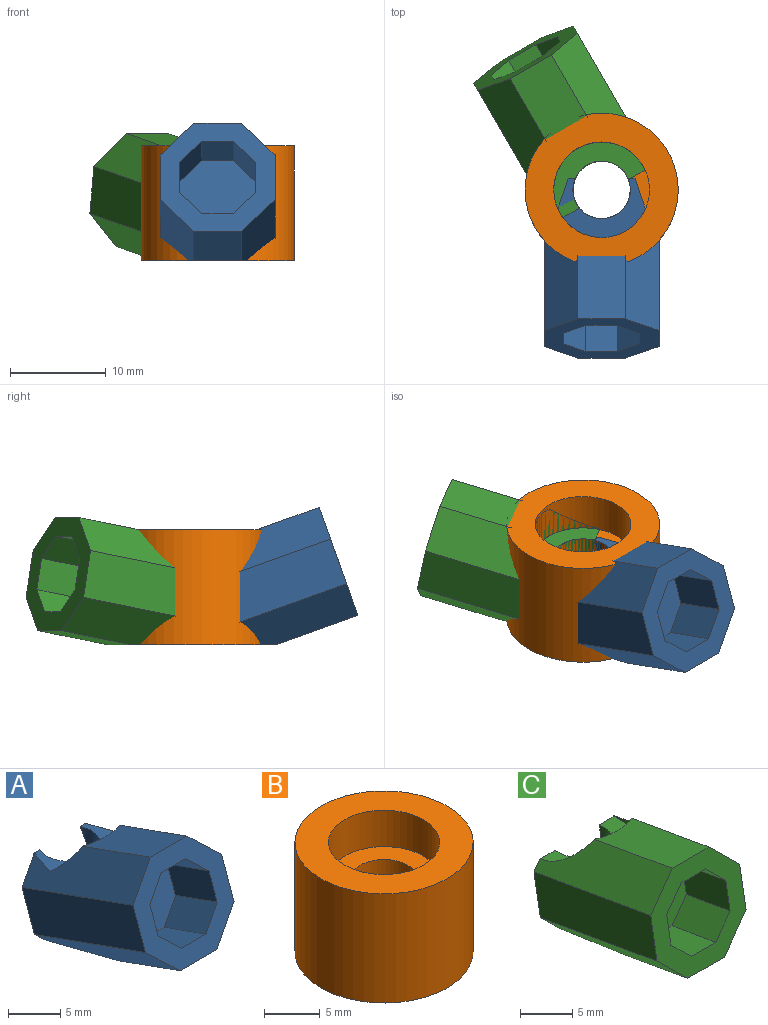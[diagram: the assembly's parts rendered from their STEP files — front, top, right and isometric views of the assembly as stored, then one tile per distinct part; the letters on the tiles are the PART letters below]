
ASSEMBLY  parts=3 mates=2
PART A: 24 faces, bbox 12x18.8x14.4 mm
  f0: plane 8x3.5mm, normal (0,0.94,-0.34), area 22.9mm2, adj f1,f8,f17,f20,f22,f23
  f1: plane 15.91x8.71mm, normal (0.71,0.24,0.67), area 67.3mm2, adj f0,f4,f17,f18,f21,f22
  f2: plane 15.91x8.71mm, normal (-0.71,0.24,0.67), area 67.3mm2, adj f3,f4,f5,f18,f21,f22
  f3: plane 8x3.5mm, normal (0,0.94,-0.34), area 22.9mm2, adj f2,f5,f6,f20,f22,f23
  f4: plane 9.16x4.97mm, normal (0,0.34,0.94), area 46mm2, adj f1,f2,f18,f21
  f5: plane 16.74x10.09mm, normal (-1,0,0), area 79.5mm2, adj f2,f3,f6,f18
  f6: plane 16.25x6.36mm, normal (-0.71,-0.24,-0.67), area 67.2mm2, adj f3,f5,f7,f18,f23
  f7: plane 8.51x4.97mm, normal (0,-0.34,-0.94), area 45mm2, adj f6,f8,f18,f23
  f8: plane 16.25x6.36mm, normal (0.71,-0.24,-0.67), area 67.2mm2, adj f0,f7,f17,f18,f23
  f9: plane 5.65x3.31mm, normal (0,-0.34,-0.94), area 19.9mm2, adj f10,f16,f18,f19
  f10: plane 6.44x4.23mm, normal (-0.71,-0.24,-0.67), area 19.9mm2, adj f9,f11,f18,f19
  f11: plane 6.77x5.15mm, normal (-1,0,0), area 19.9mm2, adj f10,f12,f18,f19
  f12: plane 6.44x4.23mm, normal (-0.71,0.24,0.67), area 19.9mm2, adj f11,f13,f18,f19
  f13: plane 5.65x3.31mm, normal (0,0.34,0.94), area 19.9mm2, adj f12,f14,f18,f19
  f14: plane 6.44x4.23mm, normal (0.71,0.24,0.67), area 19.9mm2, adj f13,f15,f18,f19
  f15: plane 6.77x5.15mm, normal (1,0,0), area 19.9mm2, adj f14,f16,f18,f19
  f16: plane 6.44x4.23mm, normal (0.71,-0.24,-0.67), area 19.9mm2, adj f9,f15,f18,f19
  f17: plane 16.74x10.09mm, normal (1,0,0), area 79.5mm2, adj f0,f1,f8,f18
  f18: plane 12x11.29mm, normal (0,-0.94,0.34), area 66.3mm2, adj f1,f2,f4,f5,f6,f7,f8,f9
  f19: plane 8x7.53mm, normal (0,-0.94,0.34), area 53mm2, adj f9,f10,f11,f12,f13,f14,f15,f16
  f20: cylinder r=3mm len=8mm, axis (0,0,1), area 71.8mm2, adj f0,f3,f22,f23
  f21: cylinder r=5mm len=9.16mm, axis (0,0,-1), area 25.9mm2, adj f1,f2,f4,f22
  f22: plane 9.16x6.22mm, normal (0,0,1), area 24.5mm2, adj f0,f1,f2,f3,f20,f21
  f23: plane 9.97x7.39mm, normal (0,0,-1), area 50.4mm2, adj f0,f3,f6,f7,f8,f20
PART B: 6 faces, bbox 16x16x12 mm
  f0: cylinder r=3mm len=8mm, axis (0,0,1), area 150.8mm2, adj f3,f5
  f1: cylinder r=8mm len=16mm, axis (0,0,-1), area 603.2mm2, adj f2,f3
  f2: plane 16x16mm, normal (0,0,1), area 122.5mm2, adj f1,f4
  f3: plane 16x16mm, normal (0,0,-1), area 172.8mm2, adj f0,f1
  f4: cylinder r=5mm len=10mm, axis (0,0,-1), area 125.7mm2, adj f2,f5
  f5: plane 10x10mm, normal (0,0,1), area 50.3mm2, adj f0,f4
PART C: 24 faces, bbox 12x17.4x13.3 mm
  f0: plane 8.07x3.15mm, normal (0,0.98,-0.17), area 21.8mm2, adj f2,f8,f17,f20,f21,f22,f23
  f1: plane 8.07x3.15mm, normal (0,0.98,-0.17), area 21.8mm2, adj f4,f5,f6,f20,f21,f22,f23
  f2: plane 15.93x6.24mm, normal (0.71,0.12,0.7), area 65.9mm2, adj f0,f3,f17,f18,f21
  f3: plane 10.5x4.97mm, normal (0,0.17,0.98), area 50.7mm2, adj f2,f4,f18,f21
  f4: plane 15.93x6.24mm, normal (-0.71,0.12,0.7), area 65.9mm2, adj f1,f3,f5,f18,f21
  f5: plane 16.62x7.67mm, normal (-1,0,0), area 79.5mm2, adj f1,f4,f6,f18
  f6: plane 16.37x4.94mm, normal (-0.71,-0.12,-0.7), area 72.6mm2, adj f1,f5,f7,f18,f23
  f7: plane 8.4x4.97mm, normal (0,-0.17,-0.98), area 42.4mm2, adj f6,f8,f18,f23
  f8: plane 16.37x4.94mm, normal (0.71,-0.12,-0.7), area 72.6mm2, adj f0,f7,f17,f18,f23
  f9: plane 5.91x3.31mm, normal (0,-0.17,-0.98), area 19.9mm2, adj f10,f16,f18,f19
  f10: plane 6.32x3.35mm, normal (-0.71,-0.12,-0.7), area 19.9mm2, adj f9,f11,f18,f19
  f11: plane 6.48x4.31mm, normal (-1,0,0), area 19.9mm2, adj f10,f12,f18,f19
  f12: plane 6.32x3.35mm, normal (-0.71,0.12,0.7), area 19.9mm2, adj f11,f13,f18,f19
  f13: plane 5.91x3.31mm, normal (0,0.17,0.98), area 19.9mm2, adj f12,f14,f18,f19
  f14: plane 6.32x3.35mm, normal (0.71,0.12,0.7), area 19.9mm2, adj f13,f15,f18,f19
  f15: plane 6.48x4.31mm, normal (1,0,0), area 19.9mm2, adj f14,f16,f18,f19
  f16: plane 6.32x3.35mm, normal (0.71,-0.12,-0.7), area 19.9mm2, adj f9,f15,f18,f19
  f17: plane 16.62x7.67mm, normal (1,0,0), area 79.5mm2, adj f0,f2,f8,f18
  f18: plane 12x11.82mm, normal (0,-0.98,0.17), area 66.3mm2, adj f2,f3,f4,f5,f6,f7,f8,f9
  f19: plane 8x7.88mm, normal (0,-0.98,0.17), area 53mm2, adj f9,f10,f11,f12,f13,f14,f15,f16
  f20: cylinder r=3mm len=8mm, axis (0,0,1), area 71.7mm2, adj f0,f1,f22,f23
  f21: cylinder r=5mm len=10mm, axis (0,0,-1), area 33.5mm2, adj f0,f1,f2,f3,f4,f22
  f22: plane 10x5.48mm, normal (0,0,1), area 27mm2, adj f0,f1,f20,f21
  f23: plane 7.61x7.59mm, normal (0,0,-1), area 39.1mm2, adj f0,f1,f6,f7,f8,f20
PLACE A at identity
PLACE B rot(axis=(0,0,-1),150deg) t=(0,0,0)mm
PLACE C rot(axis=(0,0,-1),150deg) t=(0,0,0)mm
MATE fastened B.f1 <-> C.f21  axis (0,0,-1) through (0,0,-6)mm
MATE revolute B.f1 <-> A.f21  axis (0,0,-1) through (0,0,-6)mm
